# Revit family: QF_GIORIK_BM720E
name_source: partatom
category: Specialty Equipment
revit_build: Autodesk Revit 2014 (Build: 20140709_2115(x64)
units: mm (PartAtom-declared; Revit-internal decimal feet)

## types (1)
- BM720E
    Apparent Power = 1100 VA
    Assembly Code = E1090320
    Cold Water Maximum Pressure = 50000.0 Pa
    Cold Water Minimum Pressure = 20000.0 Pa
    Cold Water Size = 1"
    Cold Water Temperature Recommended = 0 °C
    Cycle = 50 Hz
    Description = ELECTRIC BAIN-MARIE ON OPEN BASE UNIT
    FL Amps = 0 A
    HP = 1.475122000000
    Indirect Waste Flow = 0.0 L/s
    Indirect Waste Size = 1/2"
    Manufacturer = GIORIK
    Max Overcurrent Protection = 0 A
    Min Ckt Ampacity = 0 A
    Model = BM720E
    Phase = 1
    URL = www.giorik.com
    URL Cutsheet = www.giorik.com
    Volts = 230 V
    Watts = 1100 W
    Weight in Pounds = 99.2079

## geometry (parser evidence)
native form markers: Blend x12, Sweep x3
no freeform markers — native parametric forms only
